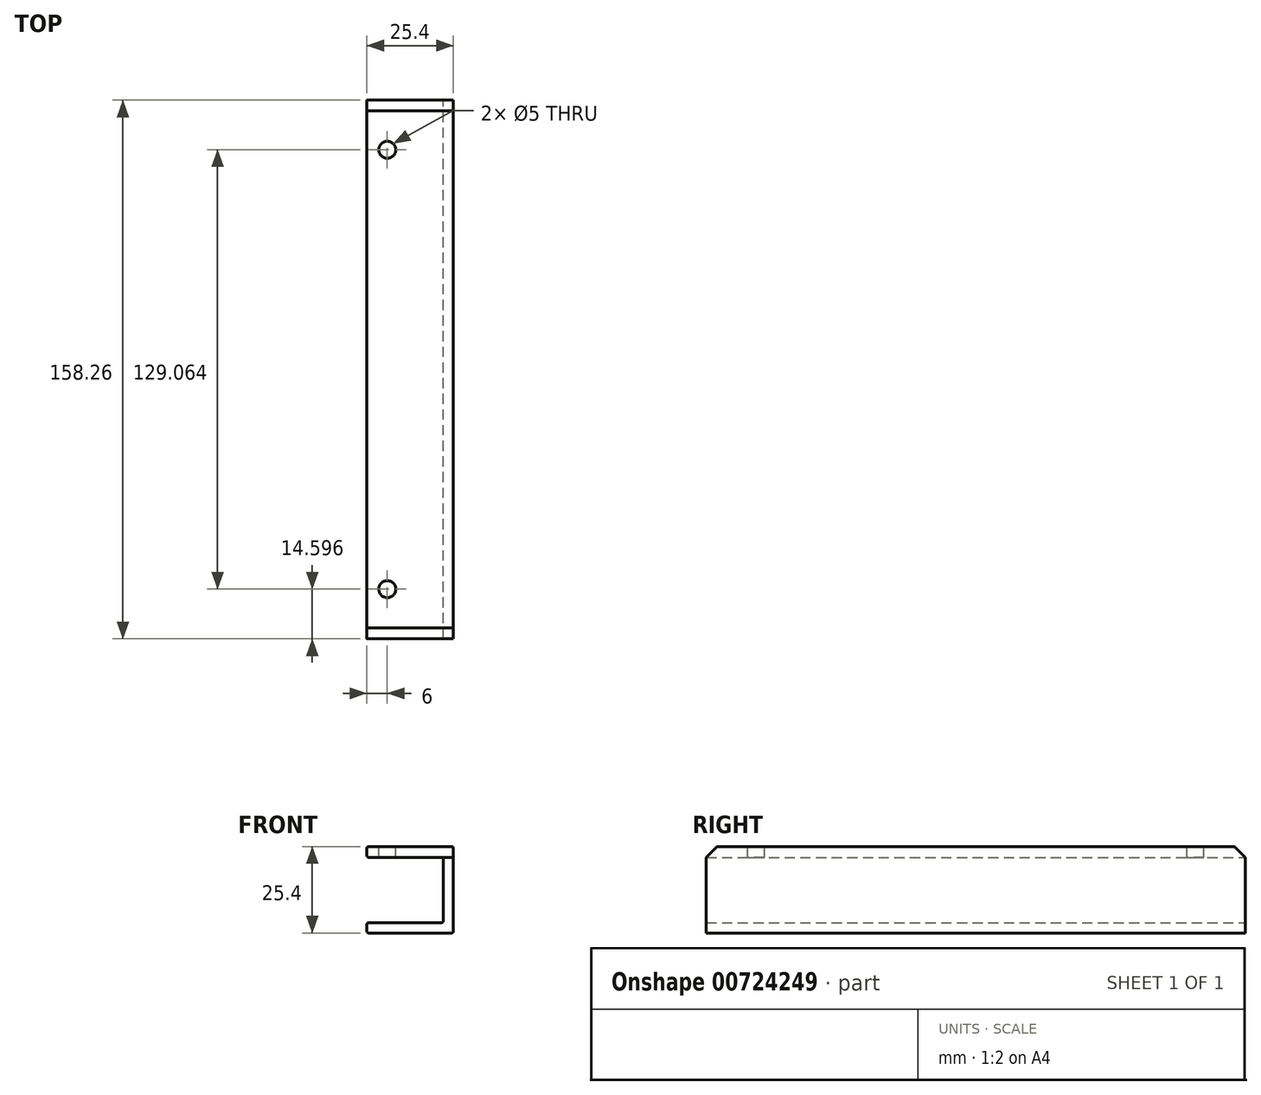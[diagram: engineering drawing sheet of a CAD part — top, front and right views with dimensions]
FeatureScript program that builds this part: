
annotation { "Feature Type Name" : "Feature", "Feature Type Description" : "" }
export const myFeature = defineFeature(function(context is Context, id is Id, definition is map)
    precondition{}
    {
        {
            var Q0;
            Q0=qCreatedBy(makeId("Front.planeOp"),FACE);
            var sketch = newSketch(context, id + "F0", { "sketchPlane" : qUnion([Q0])});
            skLineSegment(sketch, "E0", {"start": v(0, 0) * mm, "end": v(25.4, 0) * mm});
            skLineSegment(sketch, "E1", {"start": v(25.4, 0) * mm, "end": v(25.4, 25.4) * mm});
            skLineSegment(sketch, "E2", {"start": v(25.4, 25.4) * mm, "end": v(0, 25.4) * mm});
            skLineSegment(sketch, "E3", {"start": v(0, 25.4) * mm, "end": v(0, 22.23) * mm});
            skLineSegment(sketch, "E4", {"start": v(0, 22.23) * mm, "end": v(22.4, 22.23) * mm});
            skLineSegment(sketch, "E5", {"start": v(22.4, 22.23) * mm, "end": v(22.4, 3) * mm});
            skLineSegment(sketch, "E6", {"start": v(22.4, 3) * mm, "end": v(0, 3) * mm});
            skLineSegment(sketch, "E7", {"start": v(0, 3) * mm, "end": v(0, 0) * mm});
            skSolve(sketch);
        }
        {
            var Q0;
            Q0=makeQuery(id+"F0.imprint","IMPRINT",FACE,{"disambiguationData":[TD([[makeQuery(id+"F0.imprint","IMPRINT",EDGE,{"derivedFrom":sQuery(id+"F0.wireOp",EDGE,"E0")}),1.0]])]});
            extrude(context, id + "F1", {"entities" : qUnion([Q0]), "depth" : 209.06 * mm, "offsetDistance" : 25 * mm});
        }
        {
            var Q0;
            Q0=makeQuery(id+"F1.opExtrude","SWEPT_FACE",FACE,{"disambiguationData":[OSD([sQuery(id+"F0.wireOp",EDGE,"E2")])]});
            var sketch = newSketch(context, id + "F2", { "sketchPlane" : qUnion([Q0])});
            skCircle(sketch, "E8", {"center": v(6, -40) * mm, "radius": 2.5 * mm});
            skCircle(sketch, "E9", {"center": v(6, -169.06) * mm, "radius": 2.5 * mm});
            skLineSegment(sketch, "E10", {"start": v(6, -169.06) * mm, "end": v(6, -40) * mm, "construction": true});
            skLineSegment(sketch, "E11", {"start": v(6, -40) * mm, "end": v(6, 0) * mm, "construction": true});
            skLineSegment(sketch, "E12", {"start": v(6, -169.06) * mm, "end": v(6, -209.06) * mm, "construction": true});
            skSolve(sketch);
        }
        {
            var Q0;
            Q0=qSketchRegion(id+"F2",true);
            extrude(context, id + "F3", {"entities" : qUnion([Q0]), "operationType" : NewBodyOperationType.REMOVE, "oppositeDirection" : true, "depth" : 5 * mm, "offsetDistance" : 25 * mm});
        }
        {
            var Q0;
            Q0=makeQuery(id+"F1.opExtrude","SWEPT_FACE",FACE,{"disambiguationData":[OSD([sQuery(id+"F0.wireOp",EDGE,"E2")])]});
            var sketch = newSketch(context, id + "F4", { "sketchPlane" : qUnion([Q0])});
            skLineSegment(sketch, "E13", {"start": v(0, 0) * mm, "end": v(25.4, -25.4) * mm, "construction": true});
            skLineSegment(sketch, "E14", {"start": v(25.4, -25.4) * mm, "end": v(25.4, 0) * mm});
            skLineSegment(sketch, "E15", {"start": v(25.4, 0) * mm, "end": v(0, 0) * mm});
            skLineSegment(sketch, "E16", {"start": v(25.4, -209.06) * mm, "end": v(0, -209.06) * mm});
            skLineSegment(sketch, "E17", {"start": v(0, -209.06) * mm, "end": v(25.4, -183.66) * mm, "construction": true});
            skLineSegment(sketch, "E18", {"start": v(25.4, -183.66) * mm, "end": v(25.4, -209.06) * mm});
            skLineSegment(sketch, "E19", {"start": v(0, -209.06) * mm, "end": v(0, -183.66) * mm});
            skLineSegment(sketch, "E20", {"start": v(0, -183.66) * mm, "end": v(25.4, -183.66) * mm});
            skLineSegment(sketch, "E21", {"start": v(25.4, -25.4) * mm, "end": v(0, -25.4) * mm});
            skLineSegment(sketch, "E22", {"start": v(0, -25.4) * mm, "end": v(0, 0) * mm});
            skSolve(sketch);
        }
        {
            var Q0;
            Q0 = qSketchRegion(id + "F4", true);
            extrude(context, id + "F5", {"entities" : qUnion([Q0]), "operationType" : NewBodyOperationType.REMOVE, "endBound" : BoundingType.THROUGH_ALL, "oppositeDirection" : true, "depth" : 25 * mm, "offsetDistance" : 25 * mm});
        }
        {
            var Q0;
            Q0=makeQuery(id+"F1.opExtrude","SWEPT_EDGE",EDGE,{"disambiguationData":[OSD([sQuery(id+"F0.wireOp",EDGE,"E6"),sQuery(id+"F0.wireOp",EDGE,"E7")])]});
            var Q1;
            Q1=makeQuery(id+"F1.opExtrude","SWEPT_EDGE",EDGE,{"disambiguationData":[OSD([sQuery(id+"F0.wireOp",EDGE,"E0"),sQuery(id+"F0.wireOp",EDGE,"E7")])]});
            var Q2;
            Q2=makeQuery(id+"F1.opExtrude","SWEPT_EDGE",EDGE,{"disambiguationData":[OSD([sQuery(id+"F0.wireOp",EDGE,"E5"),sQuery(id+"F0.wireOp",EDGE,"E6")])]});
            var Q3;
            Q3=makeQuery(id+"F1.opExtrude","SWEPT_EDGE",EDGE,{"disambiguationData":[OSD([sQuery(id+"F0.wireOp",EDGE,"E3"),sQuery(id+"F0.wireOp",EDGE,"E4")])]});
            var Q4;
            Q4=makeQuery(id+"F1.opExtrude","SWEPT_EDGE",EDGE,{"disambiguationData":[OSD([sQuery(id+"F0.wireOp",EDGE,"E2"),sQuery(id+"F0.wireOp",EDGE,"E3")])]});
            var Q5;
            Q5=makeQuery(id+"F1.opExtrude","SWEPT_EDGE",EDGE,{"disambiguationData":[OSD([sQuery(id+"F0.wireOp",EDGE,"E4"),sQuery(id+"F0.wireOp",EDGE,"E5")])]});
            var Q6;
            Q6=makeQuery(id+"F1.opExtrude","SWEPT_EDGE",EDGE,{"disambiguationData":[OSD([sQuery(id+"F0.wireOp",EDGE,"E1"),sQuery(id+"F0.wireOp",EDGE,"E2")])]});
            var Q7;
            Q7=makeQuery(id+"F1.opExtrude","SWEPT_EDGE",EDGE,{"disambiguationData":[OSD([sQuery(id+"F0.wireOp",EDGE,"E0"),sQuery(id+"F0.wireOp",EDGE,"E1")])]});
            fillet(context, id + "F6", {"entities" : qUnion([Q0, Q1, Q2, Q3, Q4, Q5, Q6, Q7]), "radius" : 0.5 * mm, "tangentPropagation" : true, "allowEdgeOverflow" : false});
        }
        {
            var Q0;
            Q0=makeQuery(id+"F1.opExtrude","SWEPT_FACE",FACE,{"disambiguationData":[OSD([sQuery(id+"F0.wireOp",EDGE,"E3")])]});
            var sketch = newSketch(context, id + "F7", { "sketchPlane" : qUnion([Q0])});
            skLineSegment(sketch, "E23", {"start": v(25.4, 22.23) * mm, "end": v(25.4, 25.4) * mm});
            skLineSegment(sketch, "E24", {"start": v(25.4, 25.4) * mm, "end": v(28.57, 25.4) * mm});
            skLineSegment(sketch, "E25", {"start": v(28.57, 25.4) * mm, "end": v(25.4, 22.23) * mm});
            skLineSegment(sketch, "E26", {"start": v(183.66, 22.23) * mm, "end": v(183.66, 25.4) * mm});
            skLineSegment(sketch, "E27", {"start": v(183.66, 25.4) * mm, "end": v(180.49, 25.4) * mm});
            skLineSegment(sketch, "E28", {"start": v(180.49, 25.4) * mm, "end": v(183.66, 22.23) * mm});
            skSolve(sketch);
        }
        {
            var Q0;
            Q0 = qSketchRegion(id + "F7", true);
            extrude(context, id + "F8", {"entities" : qUnion([Q0]), "operationType" : NewBodyOperationType.REMOVE, "endBound" : BoundingType.THROUGH_ALL, "oppositeDirection" : true, "depth" : 25 * mm, "offsetDistance" : 25 * mm});
        }
    });
